# Revit family: CENTUM Spannschuh L XL200
name_source: partatom
category: HLS-Bauteile
revit_build: Autodesk Revit 2017 (Build: 20190508_0315(x64)
units: mm (PartAtom-declared; Revit-internal decimal feet)

## family parameters
Arbeitsebenenbasiert = Ja
Beim Laden mit Abzugskörper schneiden = Nein
Bemaßung runder Anschluss = Durchmesser verwenden
Gemeinsam genutzt = Ja
Immer vertikal = Nein
Raumberechnungspunkt = Nein
Teiletyp = Normal

## types (1)
- Centum Spannschuh L XL200
    Artikelnummer = 1662004010
    EAN = 4250928449931
    Fabrikat = MEFA
    Firma = MEFA Befestigungs- und Montagesysteme GmbH
    Gewicht = 7.22 kg
    Gewicht pro Bauteil = 7.22 kg
    Kurztext1 = Spannschuh CENTUM L
    Kurztext2 = für Profiltyp XL 200
    Material = Stahl
    Mengeneinheit = Set
    Oberflaeche = feuerstückverzinkt
    Profiltyp = XL 200
    Sicherheitsfaktor = 1.54
    Vorgabe-Ansicht = 1219 mm
    max. zul. Last Fx = 20.00 kN
    max. zul. Last Fy = 4.20 kN
    max. zul. Last Fz = 22.50 kN
    max. zul. Querlast = 0.00 kN-m
    min. Klemmdicke = 19 mm
    vpe = 1

## geometry (parser evidence)
native form markers: Sweep x6
no freeform markers — native parametric forms only
